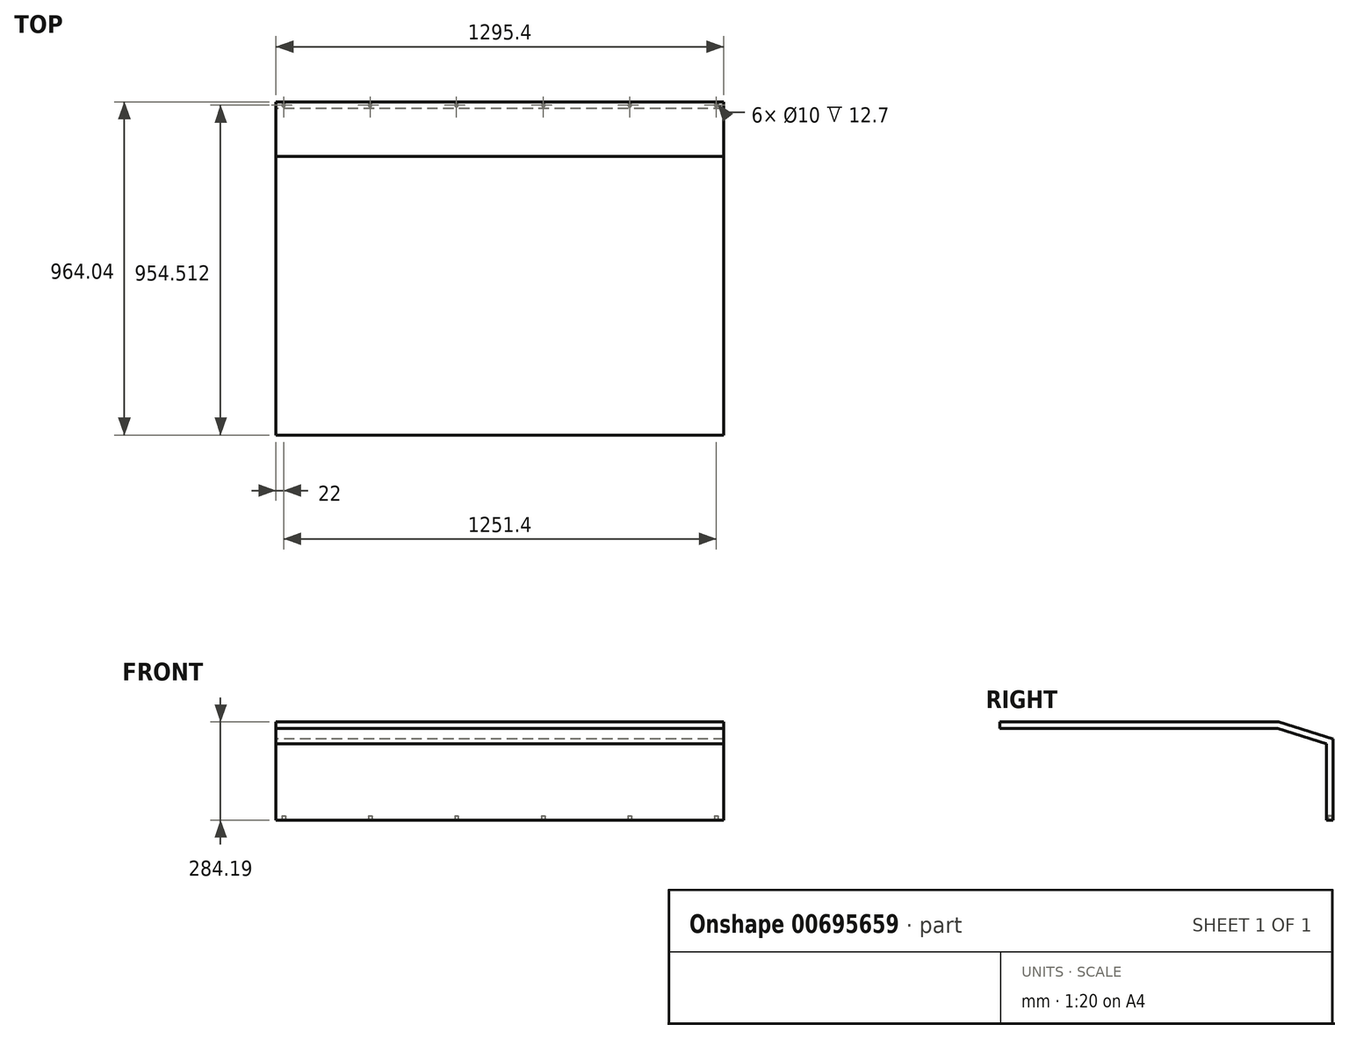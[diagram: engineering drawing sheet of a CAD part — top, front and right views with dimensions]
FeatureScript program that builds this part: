
annotation { "Feature Type Name" : "Feature", "Feature Type Description" : "" }
export const myFeature = defineFeature(function(context is Context, id is Id, definition is map)
    precondition{}
    {
        {
            var Q0;
            Q0=qCreatedBy(makeId("Right.planeOp"),FACE);
            var sketch = newSketch(context, id + "F0", { "sketchPlane" : qUnion([Q0])});
            skLineSegment(sketch, "E0", {"start": v(-507.98, 202.2) * mm, "end": v(-507.98, 183.14) * mm});
            skLineSegment(sketch, "E1", {"start": v(-507.98, 183.14) * mm, "end": v(295.56, 183.14) * mm});
            skLineSegment(sketch, "E2", {"start": v(295.56, 183.14) * mm, "end": v(437, 138.94) * mm});
            skLineSegment(sketch, "E3", {"start": v(437, 138.94) * mm, "end": v(437, -82) * mm});
            skLineSegment(sketch, "E4", {"start": v(437, -82) * mm, "end": v(456.06, -82) * mm});
            skLineSegment(sketch, "E5", {"start": v(456.06, -82) * mm, "end": v(456.06, 152.95) * mm});
            skLineSegment(sketch, "E6", {"start": v(456.06, 152.95) * mm, "end": v(298.47, 202.2) * mm});
            skLineSegment(sketch, "E7", {"start": v(298.47, 202.2) * mm, "end": v(-507.98, 202.2) * mm});
            skSolve(sketch);
        }
        {
            var Q0;
            Q0 = qSketchRegion(id + "F0", true);
            extrude(context, id + "F1", {"entities" : qUnion([Q0]), "depth" : 1295.4 * mm, "offsetDistance" : 25.4 * mm});
        }
        {
            var Q0;
            Q0=makeQuery(id+"F1.opExtrude","SWEPT_FACE",FACE,{"disambiguationData":[OSD([sQuery(id+"F0.wireOp",EDGE,"E4")])]});
            var sketch = newSketch(context, id + "F2", { "sketchPlane" : qUnion([Q0])});
            skCircle(sketch, "E8", {"center": v(22, -446.53) * mm, "radius": 5 * mm});
            skCircle(sketch, "E9", {"center": v(1273.4, -446.53) * mm, "radius": 5 * mm});
            skCircle(sketch, "E10", {"center": v(1023.4, -446.53) * mm, "radius": 5 * mm});
            skCircle(sketch, "E11", {"center": v(272, -446.53) * mm, "radius": 5 * mm});
            skCircle(sketch, "E12", {"center": v(773.4, -446.53) * mm, "radius": 5 * mm});
            skCircle(sketch, "E13", {"center": v(522, -446.53) * mm, "radius": 5 * mm});
            skSolve(sketch);
        }
        {
            var Q0;
            Q0 = qSketchRegion(id + "F2", true);
            extrude(context, id + "F3", {"entities" : qUnion([Q0]), "operationType" : NewBodyOperationType.REMOVE, "oppositeDirection" : true, "depth" : 12.7 * mm, "offsetDistance" : 25.4 * mm});
        }
    });
